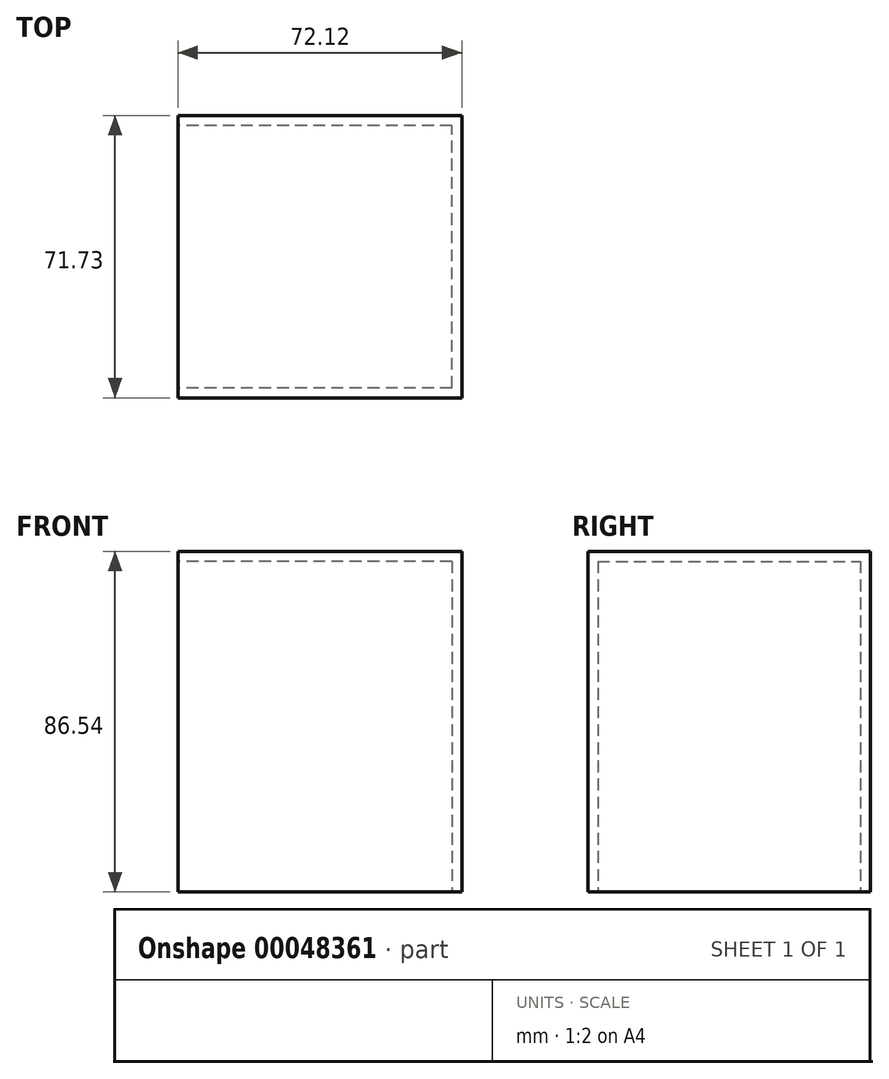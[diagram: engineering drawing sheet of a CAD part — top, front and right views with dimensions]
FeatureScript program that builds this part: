
annotation { "Feature Type Name" : "Feature", "Feature Type Description" : "" }
export const myFeature = defineFeature(function(context is Context, id is Id, definition is map)
    precondition{}
    {
        {
            var Q0;
            Q0=qCreatedBy(makeId("Front.planeOp"),FACE);
            var sketch = newSketch(context, id + "F0", { "sketchPlane" : qUnion([Q0])});
            skLineSegment(sketch, "E0.bottom", {"start": v(20.9, 37.19) * mm, "end": v(-51.2, 37.19) * mm});
            skLineSegment(sketch, "E0.top", {"start": v(20.9, -49.35) * mm, "end": v(-51.2, -49.35) * mm});
            skLineSegment(sketch, "E0.left", {"start": v(20.9, 37.19) * mm, "end": v(20.9, -49.35) * mm});
            skLineSegment(sketch, "E0.right", {"start": v(-51.2, 37.19) * mm, "end": v(-51.2, -49.35) * mm});
            skSolve(sketch);
        }
        {
            var Q0;
            Q0=makeQuery(id+"F0.imprint","IMPRINT",FACE,{"disambiguationData":[TD([[makeQuery(id+"F0.imprint","IMPRINT",EDGE,{"derivedFrom":sQuery(id+"F0.wireOp",EDGE,"E0.bottom")}),1.0]])]});
            extrude(context, id + "F1", {"entities" : qUnion([Q0]), "depth" : 71.73 * mm});
        }
        {
            var Q0;
            Q0=makeQuery(id+"F1.opExtrude","SWEPT_FACE",FACE,{"disambiguationData":[OSD([sQuery(id+"F0.wireOp",EDGE,"E0.top")])]});
            var Q1;
            Q1=makeQuery(id+"F1.opExtrude","SWEPT_FACE",FACE,{"disambiguationData":[OSD([sQuery(id+"F0.wireOp",EDGE,"E0.right")])]});
            shell(context, id + "F2", {"entities" : qUnion([Q0, Q1]), "thickness" : 2.54 * mm});
        }
    });
